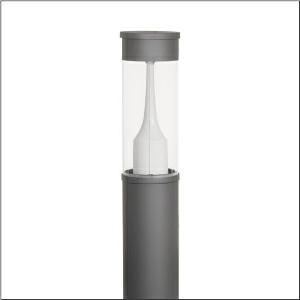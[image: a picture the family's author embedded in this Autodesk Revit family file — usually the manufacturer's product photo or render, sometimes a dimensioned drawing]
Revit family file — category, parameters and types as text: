
# Revit family: city-light_400_iq___st1_2a_5xa5305kf14h_7e7c
name_source: partatom
category: Lighting Fixtures
units: mm (PartAtom-declared; Revit-internal decimal feet)

## family parameters
Cut with Voids When Loaded = No
Host = Face
Light Source = No
Part Type = Normal
Room Calculation Point = No
Round Connector Dimension = Use Diameter
Shared = No

## types (1)
- --- (1 x LED, 1540 lm, 10 W, 4000K)
    Apparent Load = 10 VA
    CIE Flux Codes = 22 61 93 96 100
    Color Rendering = 70
    Color Temperature = 4000K
    Default Elevation = 1800 mm
    Description = City-Light 400 iQ, light pillar, Module 540 iQ-SR, primary light control with 3 zone facetted reflector, of plastic, silver coated, highly specular, structured, primary optical cover: cover, of PMMA, transparent, partly coated, light distribution: ST1.2a, primary light characteristic: asymmetric, LED, High Power LED, rated luminous flux: 1.540lm, luminous efficacy: 154lm/W, light colour: 740, colour temperature: 4000K, control gear: ECG iQ, control: presetting dimming logarithmic, Street-Remote, Auto-Match, Temp-Guard, Lumen-Switch, Night-Set, Smart-Wire, Light-Fading, Desk-Remote (wireless, voltage-free reading and setting of iQ features in the workshop via application-optimized NFC function/RFID function), optimised constant luminous flux control (CLO 2.0), with terminal, 6-pole, max. 2.5mm², mains connection: 230..240V, AC, 50/60Hz, start of lifetime: 10W, end of service life: 10W, reduction: 5W, luminaire housing, cylindrical, of extruded aluminium section, coated, Siteco® metallic grey (DB 702S), length: 4.694mm, diameter: 200mm, Module 540 iQ-SR, traffic white (RAL 9016), equipment: standard, protection rating (complete): IP65, insulation class (complete): insulation class II (safety insulation), certification: CE, ENEC, VDE, packaging unit: 1 piece

Light Distribution: ST1.2a
    Height = 500 mm
    Lamp = 1 x LED
    Lamp Light Flux = 1540 lm
    Lamp Power = 10 W
    Lamp count = 1
    Length = 200 mm  [stored 0.656168 ft]
    Luminous efficacy = 154 lm/W
    Manufacturer = Siteco
    ModVariant = No
    Model = 5XA5305KF14H
    Mounting Place = Floor
    Mounting Type = Freestanding
    Number of Poles = 1
    OnlyDefault = Yes
    Power Factor = 1
    Product Name = City-Light 400 iQ | ST1.2a
    Product group = light pillar
    ProductGroupID = 1303
    Protection Class = Protection class II
    Protection Degree = IP 65
    RLX_Detail_Level = 1
    RLX_Emergency_Light_Flux = 0 lm
    RLX_Emergency_Type = 0
    RLX_Emergency_Type_DB = No
    RlxData = <blob elided: 87317 chars, md5=798c01e4>
    Socket = socket
    Standby Power = 0 W
    System Light Flux = 1540 lm
    System Power = 10 W
    Type Comments = factory setting: luminous flux: 100 % | dim-lin: 254 | 401 mA
    Type Image = l_1006914.jpg
    URL = http://relux.com
    VarID = @adj_109249
    Voltage = 0 V
    Weight = 0.00 kg
    Width = 0 mm  [stored 0 ft]

note: [stored X ft] marks values corroborated as IEEE doubles in the binary element streams (Revit-internal decimal feet)

## geometry (parser evidence)
native form markers: Blend x4, Sweep x11
no freeform markers — native parametric forms only
